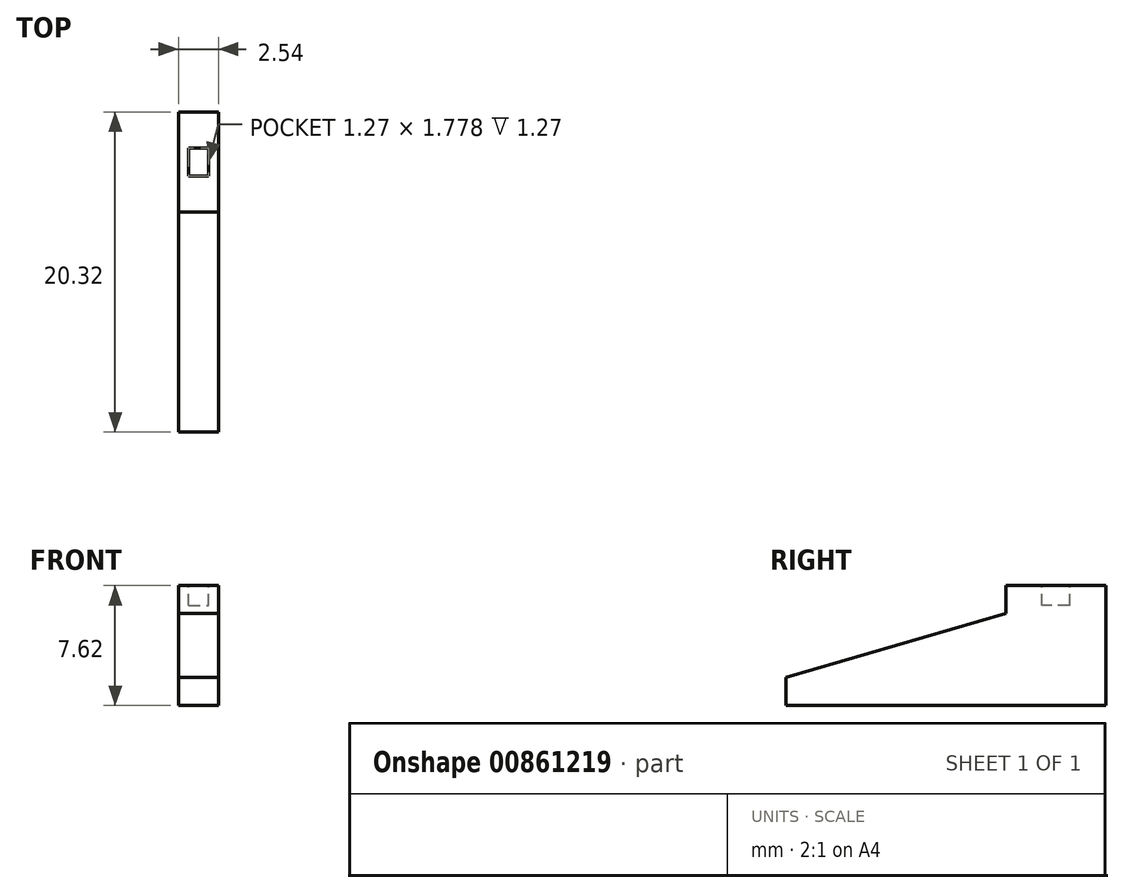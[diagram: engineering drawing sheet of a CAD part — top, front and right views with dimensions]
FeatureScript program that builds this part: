
annotation { "Feature Type Name" : "Feature", "Feature Type Description" : "" }
export const myFeature = defineFeature(function(context is Context, id is Id, definition is map)
    precondition{}
    {
        {
            var Q0;
            Q0=qCreatedBy(makeId("Right.planeOp"),FACE);
            var sketch = newSketch(context, id + "F0", { "sketchPlane" : qUnion([Q0])});
            skLineSegment(sketch, "E0", {"start": v(-13.97, 0) * mm, "end": v(6.35, 0) * mm});
            skLineSegment(sketch, "E1", {"start": v(6.35, 0) * mm, "end": v(6.35, 7.62) * mm});
            skLineSegment(sketch, "E2", {"start": v(6.35, 7.62) * mm, "end": v(0, 7.62) * mm});
            skLineSegment(sketch, "E3", {"start": v(0, 7.62) * mm, "end": v(0, 5.84) * mm});
            skLineSegment(sketch, "E4", {"start": v(-13.97, 0) * mm, "end": v(-13.97, 1.78) * mm});
            skLineSegment(sketch, "E5", {"start": v(-13.97, 1.78) * mm, "end": v(0, 5.84) * mm});
            skSolve(sketch);
        }
        {
            var Q0;
            Q0 = qSketchRegion(id + "F0", true);
            extrude(context, id + "F1", {"entities" : qUnion([Q0]), "endBound" : BoundingType.SYMMETRIC, "depth" : 2.54 * mm, "offsetDistance" : 25.4 * mm});
        }
        {
            var Q0;
            Q0=qCreatedBy(makeId("Top.planeOp"),FACE);
            cPlane(context, id + "F2", {"entities" : qUnion([Q0]), "cplaneType" : CPlaneType.OFFSET, "offset" : 7.62 * mm, "width" : 152.4 * mm, "height" : 152.4 * mm});
        }
        {
            var Q0;
            Q0=qCreatedBy(id+"F2.planeOp",FACE);
            var sketch = newSketch(context, id + "F3", { "sketchPlane" : qUnion([Q0])});
            skLineSegment(sketch, "E6.bottom", {"start": v(-0.64, 4.06) * mm, "end": v(0.64, 4.06) * mm});
            skLineSegment(sketch, "E6.top", {"start": v(-0.64, 2.29) * mm, "end": v(0.64, 2.29) * mm});
            skLineSegment(sketch, "E6.left", {"start": v(-0.64, 4.06) * mm, "end": v(-0.64, 2.29) * mm});
            skLineSegment(sketch, "E6.right", {"start": v(0.64, 4.06) * mm, "end": v(0.64, 2.29) * mm});
            skSolve(sketch);
        }
        {
            var Q0;
            Q0 = qSketchRegion(id + "F3", true);
            extrude(context, id + "F4", {"entities" : qUnion([Q0]), "operationType" : NewBodyOperationType.REMOVE, "oppositeDirection" : true, "depth" : 1.27 * mm, "offsetDistance" : 25.4 * mm});
        }
    });
